# Revit family: M-80
name_source: partatom
category: Двери
revit_build: Autodesk Revit 2016 (Build: 20160314_0715(x64)
units: mm (PartAtom-declared; Revit-internal decimal feet)

## family parameters
Всегда вертикально = Да
Заголовок OmniClass = Doors
Номер OmniClass = 23.30.10.00
Общий = Нет
Основа = Стена
При загрузке вырезать с полостями = Нет
Точка расчета площади = Нет

## types (1)
- Рулонные ворота М-80
    ADSK_URL страницы изделия = https://www.fire-tec.ru
    ADSK_Завод-изготовитель = Firetechnics
    ADSK_Наименование = Рулонные ворота из стального профиля без перфорации М-80
    ADSK_Обозначение = М-80
    ADSK_Предел огнестойкости = EI60
    ADSK_Размер_Высота = 4000 мм
    ADSK_Размер_Ширина = 3000 мм
    BL_ВысотаКороба = 180 мм
    BL_ВысотаКрепежа = 4180 мм
    BL_ДлинаНаправляющей = 90 мм
    BL_МатериалНаправляющих = BL_Сталь_Оцинкованная_Листовая_Firetechnics
    BL_МатериалПолотна = BL_Полотно_ОцинкованнаяСтали_ ПорошковойПокраскойпоRAL_Firetechnics
    BL_ОтстаяниеотДвигателя = 330 мм
    BL_ТолщинаРулона = 90 мм
    BL_ШиринаBерхнейНаправляющей = 374 мм
    BL_ШиринаBходаПолотна = 40 мм
    BL_ШиринаНаправляющих = 35 мм
    BL_ШиринаПолотна = 17 мм
    BL_ШиринапоНаправляющим = 3300 мм
    URL = https://www.fire-tec.ru
    Аналитическая конструкция = <Нет>
    Высота = 4000 мм
    Замыкание стены = По основе
    Изготовитель = Firetechnics
    Масса квадратного метра полотна = 8.60 кг
    Масса погонного метра профиля = 0.64 кг
    Огнестойкость = EI60
    Полотно Открыто = Да
    Функция = Внутренние слои
    Ширина = 3000 мм

## geometry (parser evidence)
native form markers: Blend x2
no freeform markers — native parametric forms only
